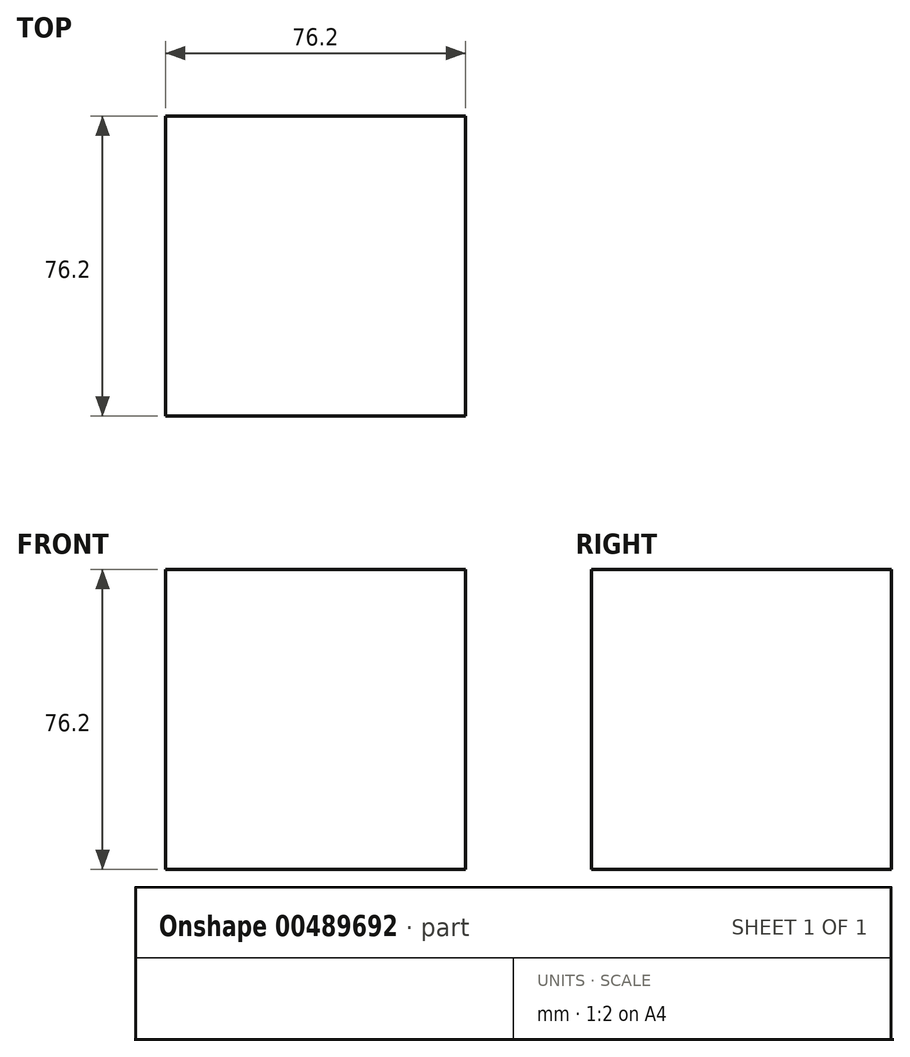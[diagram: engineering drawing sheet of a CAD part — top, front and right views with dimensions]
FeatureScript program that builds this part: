
annotation { "Feature Type Name" : "Feature", "Feature Type Description" : "" }
export const myFeature = defineFeature(function(context is Context, id is Id, definition is map)
    precondition{}
    {
        {
            var Q0;
            Q0=qCreatedBy(makeId("Right.planeOp"),FACE);
            var sketch = newSketch(context, id + "F0", { "sketchPlane" : qUnion([Q0])});
            skLineSegment(sketch, "E0", {"start": v(38.63, 64.42) * mm, "end": v(-37.57, 64.42) * mm});
            skLineSegment(sketch, "E1", {"start": v(-37.57, 64.42) * mm, "end": v(-37.57, -11.78) * mm});
            skLineSegment(sketch, "E2", {"start": v(-37.57, -11.78) * mm, "end": v(38.63, -11.78) * mm});
            skLineSegment(sketch, "E3", {"start": v(38.63, -11.78) * mm, "end": v(38.63, 64.42) * mm});
            skSolve(sketch);
        }
        {
            var Q0;
            Q0=makeQuery(id+"F0.imprint","IMPRINT",FACE,{"disambiguationData":[TD([[makeQuery(id+"F0.imprint","IMPRINT",EDGE,{"derivedFrom":sQuery(id+"F0.wireOp",EDGE,"E0")}),1.0]])]});
            extrude(context, id + "F1", {"entities" : qUnion([Q0]), "endBound" : BoundingType.SYMMETRIC, "depth" : 76.2 * mm});
        }
    });
